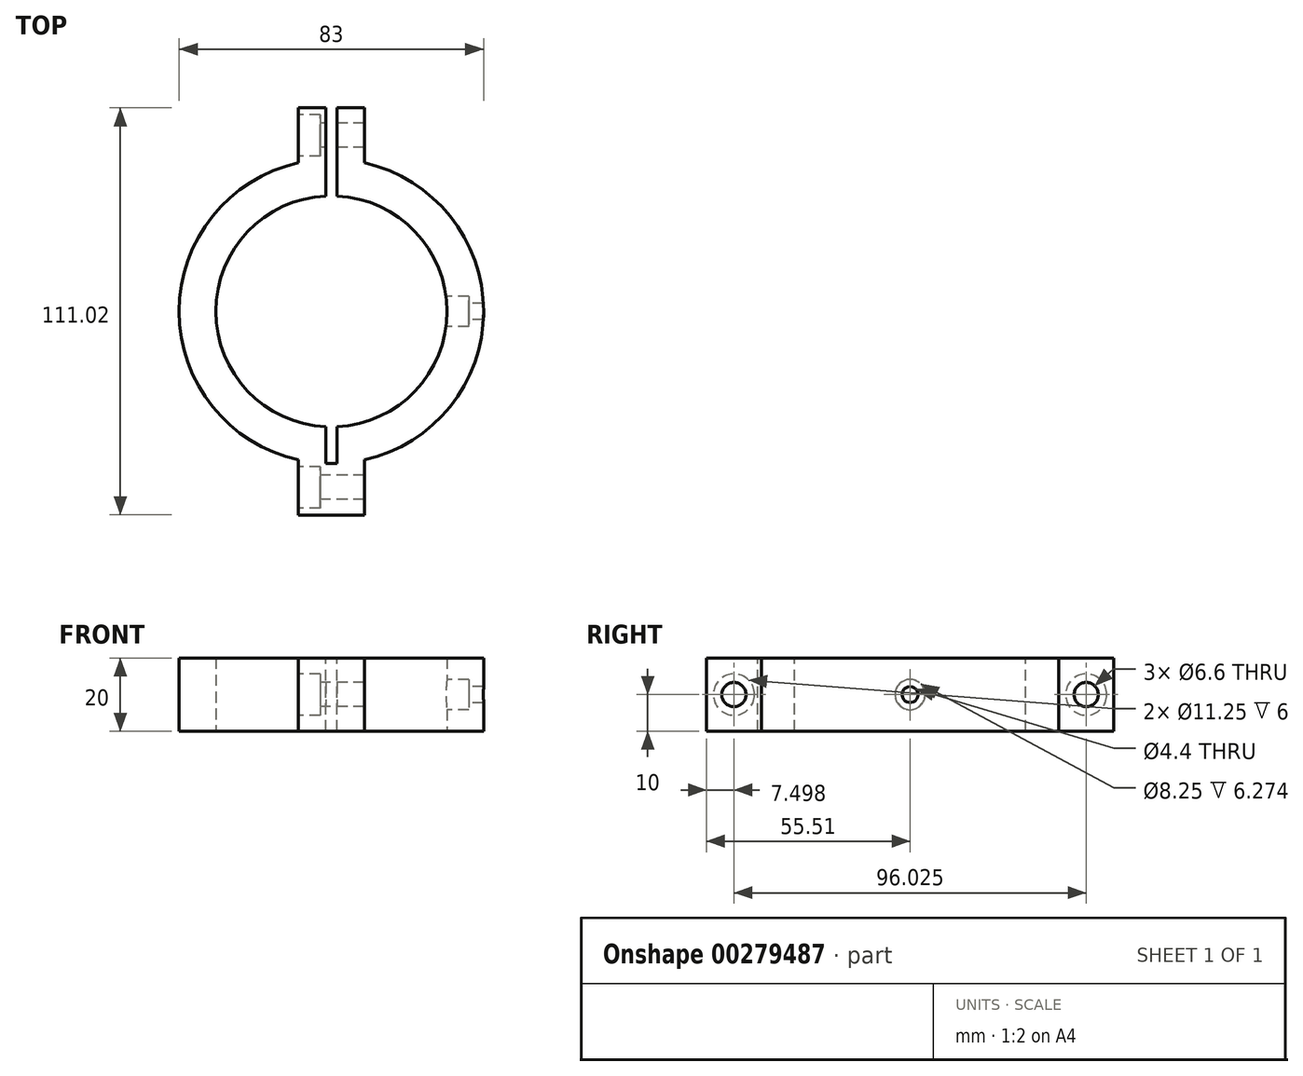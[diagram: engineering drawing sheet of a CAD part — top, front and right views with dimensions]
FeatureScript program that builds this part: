
annotation { "Feature Type Name" : "Feature", "Feature Type Description" : "" }
export const myFeature = defineFeature(function(context is Context, id is Id, definition is map)
    precondition{}
    {
        {
            var Q0;
            Q0=qCreatedBy(makeId("Top.planeOp"),FACE);
            var sketch = newSketch(context, id + "F0", { "sketchPlane" : qUnion([Q0])});
            skCircle(sketch, "E0", {"center": v(0, 0) * mm, "radius": 31.5 * mm});
            skCircle(sketch, "E1", {"center": v(0, 0) * mm, "radius": 41.5 * mm});
            skLineSegment(sketch, "E2.bottom", {"start": v(-9, 40.51) * mm, "end": v(9, 40.51) * mm});
            skLineSegment(sketch, "E2.top", {"start": v(-9, 55.51) * mm, "end": v(9, 55.51) * mm});
            skLineSegment(sketch, "E2.left", {"start": v(-9, 40.51) * mm, "end": v(-9, 55.51) * mm});
            skLineSegment(sketch, "E2.right", {"start": v(9, 40.51) * mm, "end": v(9, 55.51) * mm});
            skPoint(sketch, "E3", {"position": v(0, 55.51) * mm});
            skLineSegment(sketch, "E4.MirrorCS", {"start": v(-9, -55.51) * mm, "end": v(9, -55.51) * mm});
            skLineSegment(sketch, "E5.MirrorCS", {"start": v(9, -40.51) * mm, "end": v(9, -55.51) * mm});
            skLineSegment(sketch, "E6.MirrorCS", {"start": v(-9, -40.51) * mm, "end": v(-9, -55.51) * mm});
            skLineSegment(sketch, "E7.MirrorCS", {"start": v(-9, -40.51) * mm, "end": v(9, -40.51) * mm});
            skSolve(sketch);
        }
        {
            var Q0;
            Q0=makeQuery(id+"F0.imprint","IMPRINT",FACE,{"disambiguationData":[TD([[makeQuery(id+"F0.imprint","IMPRINT",EDGE,{"derivedFrom":sQuery(id+"F0.wireOp",EDGE,"E0")}),-1.0]])]});
            var Q1;
            Q1=makeQuery(id+"F0.imprint","IMPRINT",FACE,{"disambiguationData":[TD([[makeQuery(id+"F0.imprint","IMPRINT",EDGE,{"derivedFrom":sQuery(id+"F0.wireOp",EDGE,"E2.top")}),-1.0]])]});
            var Q2;
            {var subQ1=sQuery(id+"F0.wireOp",EDGE,"E5.MirrorCS");Q2=makeQuery(id+"F0.imprint","IMPRINT",FACE,{"disambiguationData":[TD([[makeQuery(id+"F0.imprint","IMPRINT",EDGE,{"derivedFrom":subQ1}),-1.0]])]});}
            var Q3;
            {var subQ0=sQuery(id+"F0.wireOp",EDGE,"E7.MirrorCS");Q3=makeQuery(id+"F0.imprint","IMPRINT",FACE,{"disambiguationData":[TD([[makeQuery(id+"F0.imprint","IMPRINT",EDGE,{"derivedFrom":subQ0}),-1.0]])]});}
            var Q4;
            {var subQ0=sQuery(id+"F0.wireOp",EDGE,"E2.bottom");Q4=makeQuery(id+"F0.imprint","IMPRINT",FACE,{"disambiguationData":[TD([[makeQuery(id+"F0.imprint","IMPRINT",EDGE,{"derivedFrom":subQ0}),1.0]])]});}
            extrude(context, id + "F1", {"entities" : qUnion([Q0, Q1, Q2, Q3, Q4]), "depth" : 10 * mm, "hasSecondDirection" : true, "secondDirectionOppositeDirection" : true, "secondDirectionDepth" : 10 * mm});
        }
        {
            var Q0;
            Q0=makeQuery(id+"F1.opExtrude","CAP_FACE",FACE,{"disambiguationData":[OSD([sQuery(id+"F0.wireOp",EDGE,"E0"),sQuery(id+"F0.wireOp",EDGE,"E1"),sQuery(id+"F0.wireOp",EDGE,"E2.top"),sQuery(id+"F0.wireOp",EDGE,"E2.left"),sQuery(id+"F0.wireOp",EDGE,"E2.right"),sQuery(id+"F0.wireOp",EDGE,"E5.MirrorCS"),sQuery(id+"F0.wireOp",EDGE,"E6.MirrorCS"),sQuery(id+"F0.wireOp",EDGE,"E4.MirrorCS")])],"isStart":false});
            var sketch = newSketch(context, id + "F2", { "sketchPlane" : qUnion([Q0])});
            skLineSegment(sketch, "E8.bottom", {"start": v(-1.5, 55.51) * mm, "end": v(1.5, 55.51) * mm});
            skLineSegment(sketch, "E8.top", {"start": v(-1.5, 31.46) * mm, "end": v(1.5, 31.46) * mm});
            skLineSegment(sketch, "E8.left", {"start": v(-1.5, 55.51) * mm, "end": v(-1.5, 31.46) * mm});
            skLineSegment(sketch, "E8.right", {"start": v(1.5, 55.51) * mm, "end": v(1.5, 31.46) * mm});
            skPoint(sketch, "E9", {"position": v(0, 55.51) * mm});
            skLineSegment(sketch, "E10.MirrorCS", {"start": v(-1.5, -31.46) * mm, "end": v(1.5, -31.46) * mm});
            skLineSegment(sketch, "E11.MirrorCS", {"start": v(-1.5, -55.51) * mm, "end": v(-1.5, -31.46) * mm});
            skLineSegment(sketch, "E12.MirrorCS", {"start": v(1.5, -55.51) * mm, "end": v(1.5, -31.46) * mm});
            skLineSegment(sketch, "E13.MirrorCS", {"start": v(-1.5, -55.51) * mm, "end": v(1.5, -55.51) * mm});
            skLineSegment(sketch, "E14.bottom", {"start": v(9, -55.51) * mm, "end": v(6.5, -55.51) * mm});
            skLineSegment(sketch, "E14.top", {"start": v(9, -40.51) * mm, "end": v(6.5, -40.51) * mm});
            skLineSegment(sketch, "E14.left", {"start": v(9, -55.51) * mm, "end": v(9, -40.51) * mm});
            skLineSegment(sketch, "E14.right", {"start": v(6.5, -55.51) * mm, "end": v(6.5, -40.51) * mm});
            skLineSegment(sketch, "E15.MirrorCS", {"start": v(9, 40.51) * mm, "end": v(6.5, 40.51) * mm});
            skLineSegment(sketch, "E16.MirrorCS", {"start": v(6.5, 55.51) * mm, "end": v(6.5, 40.51) * mm});
            skLineSegment(sketch, "E17.MirrorCS", {"start": v(9, 55.51) * mm, "end": v(6.5, 55.51) * mm});
            skLineSegment(sketch, "E18.MirrorCS", {"start": v(9, 55.51) * mm, "end": v(9, 40.51) * mm});
            skCircle(sketch, "E19.1", {"center": v(0, 0) * mm, "radius": 41.5 * mm});
            skLineSegment(sketch, "E19.3", {"start": v(-9, 55.51) * mm, "end": v(9, 55.51) * mm});
            skLineSegment(sketch, "E19.4", {"start": v(-9, 40.51) * mm, "end": v(-9, 55.51) * mm});
            skLineSegment(sketch, "E19.5", {"start": v(9, 40.51) * mm, "end": v(9, 55.51) * mm});
            skLineSegment(sketch, "E19.7", {"start": v(-9, -55.51) * mm, "end": v(9, -55.51) * mm});
            skLineSegment(sketch, "E19.8", {"start": v(9, -40.51) * mm, "end": v(9, -55.51) * mm});
            skLineSegment(sketch, "E19.9", {"start": v(-9, -55.51) * mm, "end": v(9, -55.51) * mm});
            skLineSegment(sketch, "E19.10", {"start": v(9, -40.51) * mm, "end": v(9, -55.51) * mm});
            skLineSegment(sketch, "E19.11", {"start": v(-9, -40.51) * mm, "end": v(-9, -55.51) * mm});
            skLineSegment(sketch, "E19.12", {"start": v(-9, -55.51) * mm, "end": v(9, -55.51) * mm});
            skSolve(sketch);
        }
        {
            var Q0;
            {var subQ0=sQuery(id+"F2.wireOp",EDGE,"E19.12");var subQ1=sQuery(id+"F2.wireOp",EDGE,"E11.MirrorCS");var subQ2=makeQuery(id+"F2.imprint","INTERSECT",VERTEX,{"derivedFrom":[subQ1,subQ0]});Q0=makeQuery(id+"F2.imprint","IMPRINT",FACE,{"disambiguationData":[TD([[makeQuery(id+"F2.imprint","IMPRINT",EDGE,{"disambiguationData":[TD([[subQ2,-1.0]])],"derivedFrom":subQ1}),-1.0]])]});}
            var Q1;
            {var subQ0=sQuery(id+"F2.wireOp",EDGE,"E19.1");var subQ1=sQuery(id+"F2.wireOp",EDGE,"E11.MirrorCS");var subQ2=makeQuery(id+"F2.imprint","INTERSECT",VERTEX,{"derivedFrom":[subQ1,subQ0]});Q1=makeQuery(id+"F2.imprint","IMPRINT",FACE,{"disambiguationData":[TD([[makeQuery(id+"F2.imprint","IMPRINT",EDGE,{"disambiguationData":[TD([[subQ2,-1.0]])],"derivedFrom":subQ1}),-1.0]])]});}
            var Q2;
            {var subQ1=sQuery(id+"F2.wireOp",EDGE,"E11.MirrorCS");var subQ4=sQuery(id+"F2.wireOp",EDGE,"E19.13");var subQ5=makeQuery(id+"F2.imprint","INTERSECT",VERTEX,{"derivedFrom":[subQ1,subQ4]});Q2=makeQuery(id+"F2.imprint","IMPRINT",FACE,{"disambiguationData":[TD([[makeQuery(id+"F2.imprint","IMPRINT",EDGE,{"disambiguationData":[TD([[subQ5,-1.0]])],"derivedFrom":subQ4}),1.0]])]});}
            var Q3;
            {var subQ5=sQuery(id+"F2.wireOp",EDGE,"E19.10");Q3=makeQuery(id+"F2.imprint","IMPRINT",FACE,{"disambiguationData":[TD([[makeQuery(id+"F2.imprint","IMPRINT",EDGE,{"derivedFrom":subQ5}),-1.0]])]});}
            var Q4;
            {var subQ0=sQuery(id+"F2.wireOp",EDGE,"E19.3");var subQ1=sQuery(id+"F2.wireOp",EDGE,"E8.left");var subQ2=makeQuery(id+"F2.imprint","INTERSECT",VERTEX,{"derivedFrom":[subQ1,subQ0]});Q4=makeQuery(id+"F2.imprint","IMPRINT",FACE,{"disambiguationData":[TD([[makeQuery(id+"F2.imprint","IMPRINT",EDGE,{"disambiguationData":[TD([[subQ2,-1.0]])],"derivedFrom":subQ1}),1.0]])]});}
            var Q5;
            {var subQ0=sQuery(id+"F2.wireOp",EDGE,"E19.1");var subQ1=sQuery(id+"F2.wireOp",EDGE,"E8.left");var subQ2=makeQuery(id+"F2.imprint","INTERSECT",VERTEX,{"derivedFrom":[subQ1,subQ0]});Q5=makeQuery(id+"F2.imprint","IMPRINT",FACE,{"disambiguationData":[TD([[makeQuery(id+"F2.imprint","IMPRINT",EDGE,{"disambiguationData":[TD([[subQ2,-1.0]])],"derivedFrom":subQ1}),1.0]])]});}
            var Q6;
            {var subQ1=sQuery(id+"F2.wireOp",EDGE,"E8.left");var subQ4=sQuery(id+"F2.wireOp",EDGE,"E19.2");var subQ5=makeQuery(id+"F2.imprint","INTERSECT",VERTEX,{"derivedFrom":[subQ1,subQ4]});Q6=makeQuery(id+"F2.imprint","IMPRINT",FACE,{"disambiguationData":[TD([[makeQuery(id+"F2.imprint","IMPRINT",EDGE,{"disambiguationData":[TD([[subQ5,-1.0]])],"derivedFrom":subQ4}),-1.0]])]});}
            var Q7;
            {var subQ5=sQuery(id+"F2.wireOp",EDGE,"E19.5");Q7=makeQuery(id+"F2.imprint","IMPRINT",FACE,{"disambiguationData":[TD([[makeQuery(id+"F2.imprint","IMPRINT",EDGE,{"derivedFrom":subQ5}),1.0]])]});}
            extrude(context, id + "F3", {"entities" : qUnion([Q0, Q1, Q2, Q3, Q4, Q5, Q6, Q7]), "operationType" : NewBodyOperationType.REMOVE, "endBound" : BoundingType.UP_TO_NEXT, "oppositeDirection" : true, "depth" : 25 * mm});
        }
        {
            var Q0;
            Q0=makeQuery(id+"F1.opExtrude","SWEPT_FACE",FACE,{"disambiguationData":[OSD([sQuery(id+"F0.wireOp",EDGE,"E2.left")])]});
            var sketch = newSketch(context, id + "F4", { "sketchPlane" : qUnion([Q0])});
            skLineSegment(sketch, "E20", {"start": v(-55.51, 0) * mm, "end": v(-40.51, 0) * mm, "construction": true});
            skPoint(sketch, "E21", {"position": v(-48.01, 0) * mm});
            skSolve(sketch);
        }
        {
            var Q0;
            Q0=makeQuery(id+"F1.opExtrude","SWEPT_FACE",FACE,{"disambiguationData":[OSD([sQuery(id+"F0.wireOp",EDGE,"E6.MirrorCS")])]});
            var sketch = newSketch(context, id + "F5", { "sketchPlane" : qUnion([Q0])});
            skLineSegment(sketch, "E22", {"start": v(40.51, 0) * mm, "end": v(55.51, 0) * mm, "construction": true});
            skPoint(sketch, "E23", {"position": v(48.01, 0) * mm});
            skSolve(sketch);
        }
        {
            var Q0;
            Q0=sQuery(id+"F4.wireOp",VERTEX,"E21");
            var Q1;
            Q1=sQuery(id+"F5.wireOp",VERTEX,"E23");
            var Q2;
            Q2=makeQuery(id+"F3.boolean.opBoolean","SPLIT",BODY,{"disambiguationData":[OD(0.0)],"derivedFrom":makeQuery(id+"F1.opExtrude","SWEPT_BODY",BODY,{"disambiguationData":[OSD([sQuery(id+"F0.wireOp",EDGE,"E0"),sQuery(id+"F0.wireOp",EDGE,"E1"),sQuery(id+"F0.wireOp",EDGE,"E2.top"),sQuery(id+"F0.wireOp",EDGE,"E2.left"),sQuery(id+"F0.wireOp",EDGE,"E2.right"),sQuery(id+"F0.wireOp",EDGE,"E5.MirrorCS"),sQuery(id+"F0.wireOp",EDGE,"E6.MirrorCS"),sQuery(id+"F0.wireOp",EDGE,"E4.MirrorCS")])]})});
            var Q3;
            Q3=makeQuery(id+"F3.boolean.opBoolean","SPLIT",BODY,{"disambiguationData":[OD(1.0)],"derivedFrom":makeQuery(id+"F1.opExtrude","SWEPT_BODY",BODY,{"disambiguationData":[OSD([sQuery(id+"F0.wireOp",EDGE,"E0"),sQuery(id+"F0.wireOp",EDGE,"E1"),sQuery(id+"F0.wireOp",EDGE,"E2.top"),sQuery(id+"F0.wireOp",EDGE,"E2.left"),sQuery(id+"F0.wireOp",EDGE,"E2.right"),sQuery(id+"F0.wireOp",EDGE,"E5.MirrorCS"),sQuery(id+"F0.wireOp",EDGE,"E6.MirrorCS"),sQuery(id+"F0.wireOp",EDGE,"E4.MirrorCS")])]})});
            hole(context, id + "F6", {"style" : HoleStyle.C_BORE, "endStyle" : HoleEndStyle.THROUGH, "standardTappedOrClearance" : lookupTablePath({ "standard" : "ISO", "fit" : "Normal", "size" : "M6", "type" : "Clearance" }), "standardBlindInLast" : lookupTablePath({ "fit" : "Standard", "standard" : "ISO", "size" : "M6", "type" : "Clearance" }), "holeDiameter" : 6.6 * mm, "cBoreDiameter" : 11.25 * mm, "cBoreDepth" : 6 * mm, "tappedDepth" : 12 * mm, "tapClearance" : 3, "locations" : qUnion([Q0, Q1]), "scope" : qUnion([Q2, Q3])});
        }
        {
            var Q0;
            Q0=qCreatedBy(makeId("Top.planeOp"),FACE);
            var sketch = newSketch(context, id + "F7", { "sketchPlane" : qUnion([Q0])});
            skPoint(sketch, "E24", {"position": v(31.5, 0) * mm});
            skLineSegment(sketch, "E25", {"start": v(31.5, 0) * mm, "end": v(0, 0) * mm, "construction": true});
            skSolve(sketch);
        }
        {
            var Q0;
            Q0=sQuery(id+"F7.wireOp",VERTEX,"E24");
            var Q1;
            Q1=sQuery(id+"F7.wireOp",EDGE,"E25");
            cPlane(context, id + "F8", {"entities" : qUnion([Q0, Q1]), "cplaneType" : CPlaneType.LINE_POINT, "offset" : 25 * mm, "width" : 150 * mm, "height" : 150 * mm});
        }
        {
            var Q0;
            Q0=qCreatedBy(id+"F8.planeOp",FACE);
            cPlane(context, id + "F9", {"entities" : qUnion([Q0]), "cplaneType" : CPlaneType.OFFSET, "offset" : 2 * mm, "width" : 150 * mm, "height" : 150 * mm});
        }
        {
            var Q0;
            Q0=qCreatedBy(id+"F9.planeOp",FACE);
            var sketch = newSketch(context, id + "F10", { "sketchPlane" : qUnion([Q0])});
            skPoint(sketch, "E26", {"position": v(0, 0) * mm});
            skSolve(sketch);
        }
        {
            var Q0;
            Q0=sQuery(id+"F10.wireOp",VERTEX,"E26");
            var Q1;
            Q1=makeQuery(id+"F3.boolean.opBoolean","SPLIT",BODY,{"disambiguationData":[OD(1.0)],"derivedFrom":makeQuery(id+"F1.opExtrude","SWEPT_BODY",BODY,{"disambiguationData":[OSD([sQuery(id+"F0.wireOp",EDGE,"E0"),sQuery(id+"F0.wireOp",EDGE,"E1"),sQuery(id+"F0.wireOp",EDGE,"E2.top"),sQuery(id+"F0.wireOp",EDGE,"E2.left"),sQuery(id+"F0.wireOp",EDGE,"E2.right"),sQuery(id+"F0.wireOp",EDGE,"E5.MirrorCS"),sQuery(id+"F0.wireOp",EDGE,"E6.MirrorCS"),sQuery(id+"F0.wireOp",EDGE,"E4.MirrorCS")])]})});
            hole(context, id + "F11", {"style" : HoleStyle.C_BORE, "endStyle" : HoleEndStyle.BLIND, "holeDiameter" : 4.4 * mm, "cBoreDiameter" : 8.25 * mm, "cBoreDepth" : 6 * mm, "holeDepth" : 14.25 * mm, "tappedDepth" : 12 * mm, "tapClearance" : 3, "locations" : qUnion([Q0]), "scope" : qUnion([Q1])});
        }
    });
